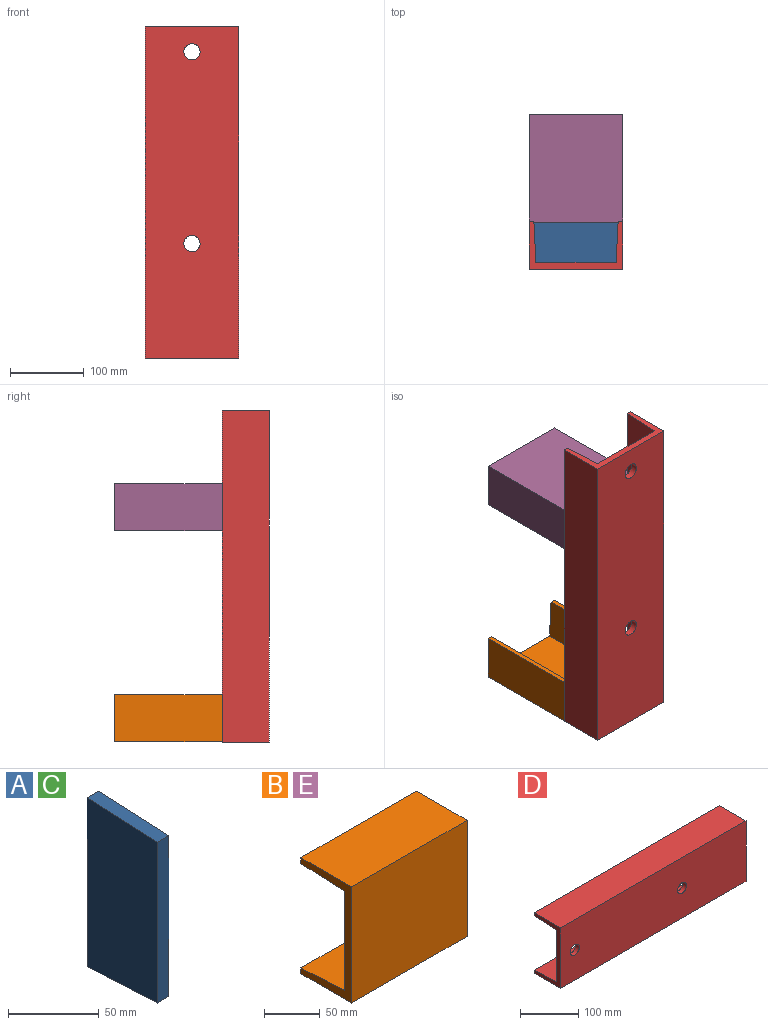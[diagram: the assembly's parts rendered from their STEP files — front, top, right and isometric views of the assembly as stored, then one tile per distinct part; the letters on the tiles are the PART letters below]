
ASSEMBLY  parts=5 mates=4
PART A: 6 faces, bbox 9.2x54.8x114.2 mm
  f0: plane 54.8x9.2mm, normal (0,-0.05,-1), area 504.8mm2, adj f1,f3,f4,f5
  f1: plane 114.2x9.2mm, normal (0,1,0), area 1050.6mm2, adj f0,f2,f4,f5
  f2: plane 54.8x9.2mm, normal (0,-0.05,1), area 504.8mm2, adj f1,f3,f4,f5
  f3: plane 108.6x9.2mm, normal (0,-1,0), area 999.1mm2, adj f0,f2,f4,f5
  f4: plane 114.2x54.8mm, normal (1,0,0), area 6104.7mm2, adj f0,f1,f2,f3
  f5: plane 114.2x54.8mm, normal (-1,0,0), area 6104.7mm2, adj f0,f1,f2,f3
PART B: 10 faces, bbox 146x64x127 mm
  f0: plane 146x6.4mm, normal (0,1,0), area 934.4mm2, adj f1,f7,f8,f9
  f1: plane 146x64mm, normal (0,0,1), area 9344mm2, adj f0,f2,f8,f9
  f2: plane 146x127mm, normal (0,-1,0), area 18542mm2, adj f1,f3,f8,f9
  f3: plane 146x64mm, normal (0,0,-1), area 9344mm2, adj f2,f4,f8,f9
  f4: plane 146x6.4mm, normal (0,1,0), area 934.4mm2, adj f3,f5,f8,f9
  f5: plane 146x54.8mm, normal (0,0.05,1), area 8011.2mm2, adj f4,f6,f8,f9
  f6: plane 146x108.6mm, normal (0,1,0), area 15855.6mm2, adj f5,f7,f8,f9
  f7: plane 146x54.8mm, normal (0,0.05,-1), area 8011.2mm2, adj f0,f6,f8,f9
  f8: plane 127x64mm, normal (1,0,0), area 2023.3mm2, adj f0,f1,f2,f3,f4,f5,f6,f7
  f9: plane 127x64mm, normal (-1,0,0), area 2023.3mm2, adj f0,f1,f2,f3,f4,f5,f6,f7
PART C: same geometry as A
PART D: 12 faces, bbox 450x64x127 mm
  f0: plane 450x6.4mm, normal (0,1,0), area 2880mm2, adj f1,f7,f8,f9
  f1: plane 450x64mm, normal (0,0,1), area 28800mm2, adj f0,f2,f8,f9
  f2: plane 450x127mm, normal (0,-1,0), area 56389.7mm2, adj f1,f3,f8,f9,f10,f11
  f3: plane 450x64mm, normal (0,0,-1), area 28800mm2, adj f2,f4,f8,f9
  f4: plane 450x6.4mm, normal (0,1,0), area 2880mm2, adj f3,f5,f8,f9
  f5: plane 450x54.8mm, normal (0,0.05,1), area 24692.2mm2, adj f4,f6,f8,f9
  f6: plane 450x108.6mm, normal (0,1,0), area 48109.7mm2, adj f5,f7,f8,f9,f10,f11
  f7: plane 450x54.8mm, normal (0,0.05,-1), area 24692.2mm2, adj f0,f6,f8,f9
  f8: plane 127x64mm, normal (1,0,0), area 2023.3mm2, adj f0,f1,f2,f3,f4,f5,f6,f7
  f9: plane 127x64mm, normal (-1,0,0), area 2023.3mm2, adj f0,f1,f2,f3,f4,f5,f6,f7
  f10: cylinder r=11mm len=22mm, axis (0,-1,0), area 635.9mm2, adj f2,f6
  f11: cylinder r=11mm len=22mm, axis (0,-1,0), area 635.9mm2, adj f2,f6
PART E: same geometry as B
PLACE A rot(axis=(0,-1,0),90deg) t=(-312.44,-538.25,290.12)mm
PLACE B rot(axis=(0.58,0.58,0.58),120deg) t=(-417.84,-144.81,-232.66)mm
PLACE C rot(axis=(0,1,0),90deg) t=(-449.73,-538.25,-41.48)mm
PLACE D rot(axis=(0,1,0),90deg) t=(-460.21,28.14,399.32)mm
PLACE E rot(axis=(-0.58,-0.58,0.58),120deg) t=(-344.33,-144.81,481.3)mm
MATE fastened A.f3 <-> D.f6  axis (0,-1,0) through (-381.09,-199.61,299.32)mm
MATE fastened B.f9 <-> C.f1  axis (0,-1,0) through (-381.09,-144.81,-50.68)mm
MATE fastened A.f1 <-> E.f9  axis (0,1,0) through (-381.09,-144.81,294.72)mm
MATE fastened C.f3 <-> D.f6  axis (0,-1,0) through (-381.09,-199.61,-50.68)mm
